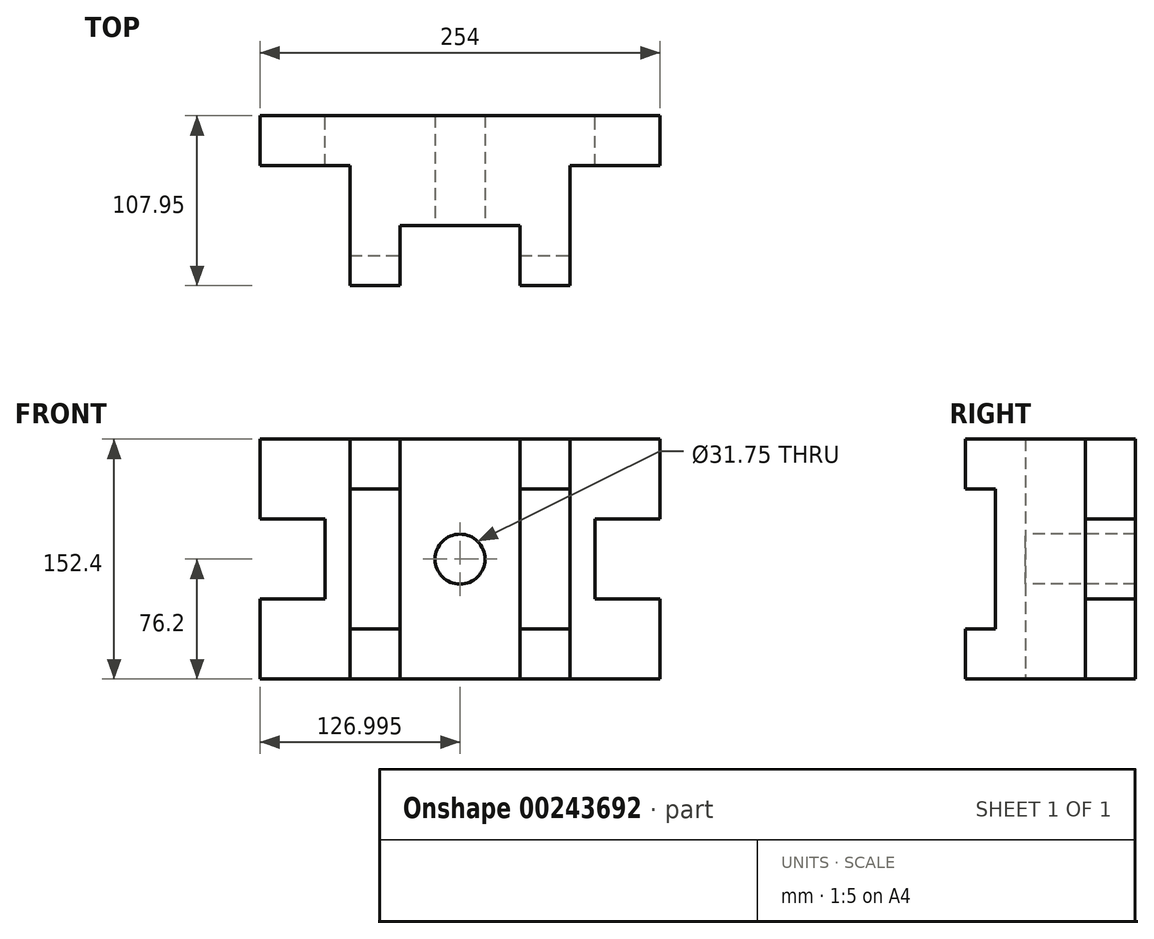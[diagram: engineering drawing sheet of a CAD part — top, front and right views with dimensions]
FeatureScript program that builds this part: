
annotation { "Feature Type Name" : "Feature", "Feature Type Description" : "" }
export const myFeature = defineFeature(function(context is Context, id is Id, definition is map)
    precondition{}
    {
        {
            var Q0;
            Q0=qCreatedBy(makeId("Front.planeOp"),FACE);
            var sketch = newSketch(context, id + "F0", { "sketchPlane" : qUnion([Q0])});
            skLineSegment(sketch, "E0.bottom", {"start": v(-74.48, 50.8) * mm, "end": v(179.52, 50.8) * mm});
            skLineSegment(sketch, "E0.top", {"start": v(-74.48, -101.6) * mm, "end": v(179.52, -101.6) * mm});
            skLineSegment(sketch, "E0.left", {"start": v(-74.48, 50.8) * mm, "end": v(-74.48, 0) * mm});
            skLineSegment(sketch, "E0.right", {"start": v(179.52, 50.8) * mm, "end": v(179.52, 0) * mm});
            skLineSegment(sketch, "E1", {"start": v(-74.48, 0) * mm, "end": v(-33.2, 0) * mm});
            skLineSegment(sketch, "E2", {"start": v(-33.2, 0) * mm, "end": v(-33.2, -50.8) * mm});
            skLineSegment(sketch, "E3", {"start": v(-33.2, -50.8) * mm, "end": v(-74.48, -50.8) * mm});
            skLineSegment(sketch, "E4.trimOffspring", {"start": v(-74.48, -50.8) * mm, "end": v(-74.48, -101.6) * mm});
            skLineSegment(sketch, "E5.MirrorCS", {"start": v(179.52, 0) * mm, "end": v(138.24, 0) * mm});
            skLineSegment(sketch, "E6.MirrorCS", {"start": v(138.24, -50.8) * mm, "end": v(179.52, -50.8) * mm});
            skLineSegment(sketch, "E7.trimOffspring", {"start": v(179.52, -50.8) * mm, "end": v(179.52, -101.6) * mm});
            skPoint(sketch, "E8.end.orphan", {"position": v(52.52, 50.8) * mm});
            skPoint(sketch, "E8.start.orphan", {"position": v(52.52, -101.6) * mm});
            skLineSegment(sketch, "E9", {"start": v(138.24, 0) * mm, "end": v(138.24, -50.8) * mm});
            skSolve(sketch);
        }
        {
            var Q0;
            Q0=makeQuery(id+"F0.imprint","IMPRINT",FACE,{"disambiguationData":[TD([[makeQuery(id+"F0.imprint","IMPRINT",EDGE,{"derivedFrom":sQuery(id+"F0.wireOp",EDGE,"E0.bottom")}),-1.0]])]});
            extrude(context, id + "F1", {"entities" : qUnion([Q0]), "depth" : 31.75 * mm});
        }
        {
            var Q0;
            Q0=makeQuery(id+"F1.opExtrude","CAP_FACE",FACE,{"disambiguationData":[OSD([sQuery(id+"F0.wireOp",EDGE,"E0.bottom"),sQuery(id+"F0.wireOp",EDGE,"E0.top"),sQuery(id+"F0.wireOp",EDGE,"E0.left"),sQuery(id+"F0.wireOp",EDGE,"E0.right"),sQuery(id+"F0.wireOp",EDGE,"E1"),sQuery(id+"F0.wireOp",EDGE,"E2"),sQuery(id+"F0.wireOp",EDGE,"E3"),sQuery(id+"F0.wireOp",EDGE,"E4.trimOffspring"),sQuery(id+"F0.wireOp",EDGE,"d02deeb2-3776-4cb6-a9ca-a12d89563ab00.MirrorCS"),sQuery(id+"F0.wireOp",EDGE,"E5.MirrorCS"),sQuery(id+"F0.wireOp",EDGE,"E6.MirrorCS"),sQuery(id+"F0.wireOp",EDGE,"E7.trimOffspring")])],"isStart":false});
            var sketch = newSketch(context, id + "F2", { "sketchPlane" : qUnion([Q0])});
            skLineSegment(sketch, "E10", {"start": v(-17.33, 50.8) * mm, "end": v(-17.33, -101.6) * mm});
            skLineSegment(sketch, "E11.MirrorCS", {"start": v(122.37, 50.8) * mm, "end": v(122.37, -101.6) * mm});
            skSolve(sketch);
        }
        {
            var Q0;
            {var subQ0=sQuery(id+"F2.wireOp",EDGE,"E10");Q0=makeQuery(id+"F2.imprint","IMPRINT",FACE,{"disambiguationData":[TD([[makeQuery(id+"F2.imprint","IMPRINT",EDGE,{"derivedFrom":subQ0}),1.0]])]});}
            extrude(context, id + "F3", {"entities" : qUnion([Q0]), "operationType" : NewBodyOperationType.ADD, "depth" : 38.1 * mm});
        }
        {
            var Q0;
            Q0=makeQuery(id+"F3.opExtrude","CAP_FACE",FACE,{"disambiguationData":[OSD([sQuery(id+"F0.wireOp",EDGE,"E0.bottom"),sQuery(id+"F0.wireOp",EDGE,"E0.top"),sQuery(id+"F2.wireOp",EDGE,"E10"),sQuery(id+"F2.wireOp",EDGE,"E11.MirrorCS")])],"isStart":false});
            var sketch = newSketch(context, id + "F4", { "sketchPlane" : qUnion([Q0])});
            skLineSegment(sketch, "E12", {"start": v(14.42, 50.8) * mm, "end": v(14.42, -101.6) * mm});
            skLineSegment(sketch, "E13", {"start": v(90.62, 50.8) * mm, "end": v(90.62, -101.6) * mm});
            skPoint(sketch, "E14.end.orphan", {"position": v(90.62, -25.4) * mm});
            skCircle(sketch, "E15", {"center": v(52.52, -25.4) * mm, "radius": 15.88 * mm});
            skPoint(sketch, "E16", {"position": v(14.42, -25.4) * mm});
            skSolve(sketch);
        }
        {
            var Q0;
            {var subQ0=sQuery(id+"F4.wireOp",EDGE,"E12");Q0=makeQuery(id+"F4.imprint","IMPRINT",FACE,{"disambiguationData":[TD([[makeQuery(id+"F4.imprint","IMPRINT",EDGE,{"derivedFrom":subQ0}),-1.0]])]});}
            var Q1;
            {var subQ0=sQuery(id+"F4.wireOp",EDGE,"E13");Q1=makeQuery(id+"F4.imprint","IMPRINT",FACE,{"disambiguationData":[TD([[makeQuery(id+"F4.imprint","IMPRINT",EDGE,{"derivedFrom":subQ0}),1.0]])]});}
            extrude(context, id + "F5", {"entities" : qUnion([Q0, Q1]), "operationType" : NewBodyOperationType.ADD, "depth" : 19.05 * mm});
        }
        {
            var Q0;
            Q0=makeQuery(id+"F4.imprint","IMPRINT",FACE,{"disambiguationData":[TD([[makeQuery(id+"F4.imprint","IMPRINT",EDGE,{"derivedFrom":sQuery(id+"F4.wireOp",EDGE,"E15")}),1.0]])]});
            extrude(context, id + "F6", {"entities" : qUnion([Q0]), "operationType" : NewBodyOperationType.REMOVE, "endBound" : BoundingType.THROUGH_ALL, "oppositeDirection" : true, "depth" : 25.4 * mm});
        }
        {
            var Q0;
            Q0=makeQuery(id+"F5.opExtrude","CAP_FACE",FACE,{"disambiguationData":[OSD([sQuery(id+"F0.wireOp",EDGE,"E0.bottom"),sQuery(id+"F0.wireOp",EDGE,"E0.top"),sQuery(id+"F2.wireOp",EDGE,"E10"),sQuery(id+"F4.wireOp",EDGE,"E12")])],"isStart":false});
            var sketch = newSketch(context, id + "F7", { "sketchPlane" : qUnion([Q0])});
            skLineSegment(sketch, "E17", {"start": v(-17.33, 19.05) * mm, "end": v(14.42, 19.05) * mm});
            skLineSegment(sketch, "E18", {"start": v(-17.33, -69.85) * mm, "end": v(14.42, -69.85) * mm});
            skLineSegment(sketch, "E19", {"start": v(-17.33, 50.8) * mm, "end": v(-17.33, 19.05) * mm});
            skLineSegment(sketch, "E20", {"start": v(-17.33, -69.85) * mm, "end": v(-17.33, -101.6) * mm});
            skSolve(sketch);
        }
        {
            var Q0;
            {var subQ0=sQuery(id+"F7.wireOp",EDGE,"E17");Q0=makeQuery(id+"F7.imprint","IMPRINT",FACE,{"disambiguationData":[TD([[makeQuery(id+"F7.imprint","IMPRINT",EDGE,{"derivedFrom":subQ0}),1.0]])]});}
            var Q1;
            {var subQ0=sQuery(id+"F7.wireOp",EDGE,"E18");Q1=makeQuery(id+"F7.imprint","IMPRINT",FACE,{"disambiguationData":[TD([[makeQuery(id+"F7.imprint","IMPRINT",EDGE,{"derivedFrom":subQ0}),-1.0]])]});}
            extrude(context, id + "F8", {"entities" : qUnion([Q0, Q1]), "operationType" : NewBodyOperationType.ADD, "depth" : 19.05 * mm});
        }
        {
            var Q0;
            Q0=makeQuery(id+"F5.opExtrude","CAP_FACE",FACE,{"disambiguationData":[OSD([sQuery(id+"F0.wireOp",EDGE,"E0.bottom"),sQuery(id+"F0.wireOp",EDGE,"E0.top"),sQuery(id+"F2.wireOp",EDGE,"E11.MirrorCS"),sQuery(id+"F4.wireOp",EDGE,"E13")])],"isStart":false});
            var sketch = newSketch(context, id + "F9", { "sketchPlane" : qUnion([Q0])});
            skLineSegment(sketch, "E21", {"start": v(90.62, 19.05) * mm, "end": v(122.37, 19.05) * mm});
            skLineSegment(sketch, "E22", {"start": v(90.62, -69.85) * mm, "end": v(122.37, -69.85) * mm});
            skLineSegment(sketch, "E23", {"start": v(122.37, -69.85) * mm, "end": v(122.37, -101.6) * mm});
            skLineSegment(sketch, "E24", {"start": v(90.62, 19.05) * mm, "end": v(90.62, 50.8) * mm});
            skSolve(sketch);
        }
        {
            var Q0;
            {var subQ0=sQuery(id+"F9.wireOp",EDGE,"E21");Q0=makeQuery(id+"F9.imprint","IMPRINT",FACE,{"disambiguationData":[TD([[makeQuery(id+"F9.imprint","IMPRINT",EDGE,{"derivedFrom":subQ0}),1.0]])]});}
            var Q1;
            {var subQ0=sQuery(id+"F9.wireOp",EDGE,"E22");Q1=makeQuery(id+"F9.imprint","IMPRINT",FACE,{"disambiguationData":[TD([[makeQuery(id+"F9.imprint","IMPRINT",EDGE,{"derivedFrom":subQ0}),-1.0]])]});}
            extrude(context, id + "F10", {"entities" : qUnion([Q0, Q1]), "operationType" : NewBodyOperationType.ADD, "depth" : 19.05 * mm});
        }
    });
